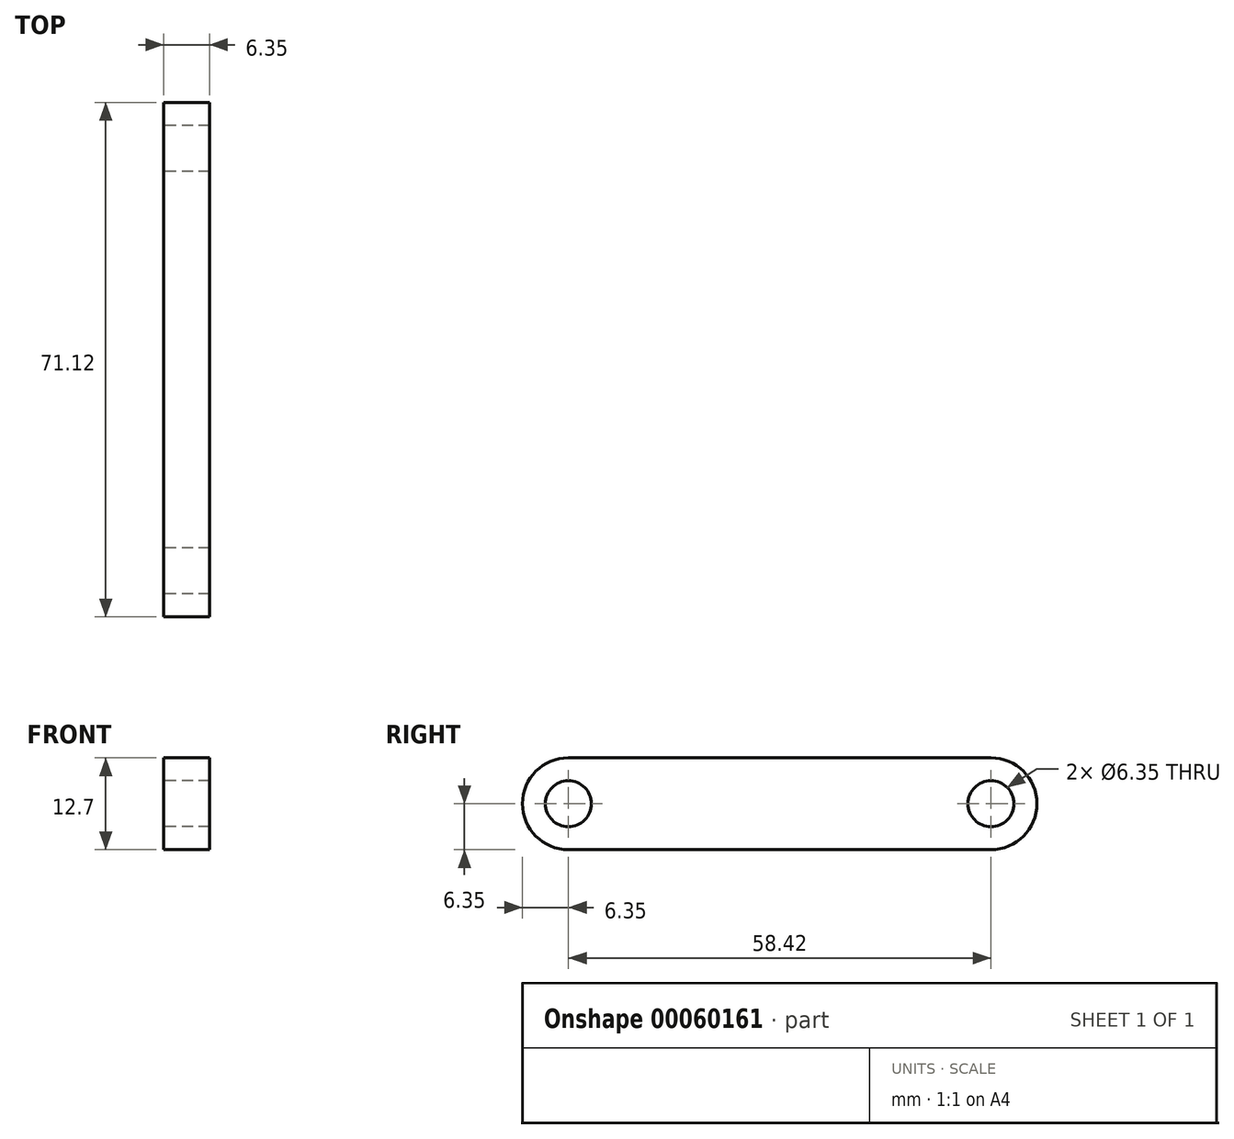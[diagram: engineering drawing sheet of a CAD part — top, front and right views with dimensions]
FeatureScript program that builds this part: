
annotation { "Feature Type Name" : "Feature", "Feature Type Description" : "" }
export const myFeature = defineFeature(function(context is Context, id is Id, definition is map)
    precondition{}
    {
        {
            var Q0;
            Q0=qCreatedBy(makeId("Right.planeOp"),FACE);
            var sketch = newSketch(context, id + "F0", { "sketchPlane" : qUnion([Q0])});
            skCircle(sketch, "E0", {"center": v(0, 0) * mm, "radius": 3.18 * mm});
            skCircle(sketch, "E1", {"center": v(-58.42, 0) * mm, "radius": 3.18 * mm});
            skArc(sketch, "E2", {"start": v(0, 6.35) * mm, "mid": v(6.35, 0) * mm, "end": v(0, -6.35) * mm});
            skArc(sketch, "E3", {"start": v(-58.42, 6.35) * mm, "mid": v(-64.77, 0) * mm, "end": v(-58.42, -6.35) * mm});
            skLineSegment(sketch, "E4", {"start": v(-58.42, 6.35) * mm, "end": v(0, 6.35) * mm});
            skLineSegment(sketch, "E5", {"start": v(0, -6.35) * mm, "end": v(-58.42, -6.35) * mm});
            skSolve(sketch);
        }
        {
            var Q0;
            Q0=makeQuery(id+"F0.imprint","IMPRINT",FACE,{"disambiguationData":[TD([[makeQuery(id+"F0.imprint","IMPRINT",EDGE,{"derivedFrom":sQuery(id+"F0.wireOp",EDGE,"E0")}),-1.0]])]});
            extrude(context, id + "F1", {"entities" : qUnion([Q0]), "depth" : 6.35 * mm});
        }
    });
